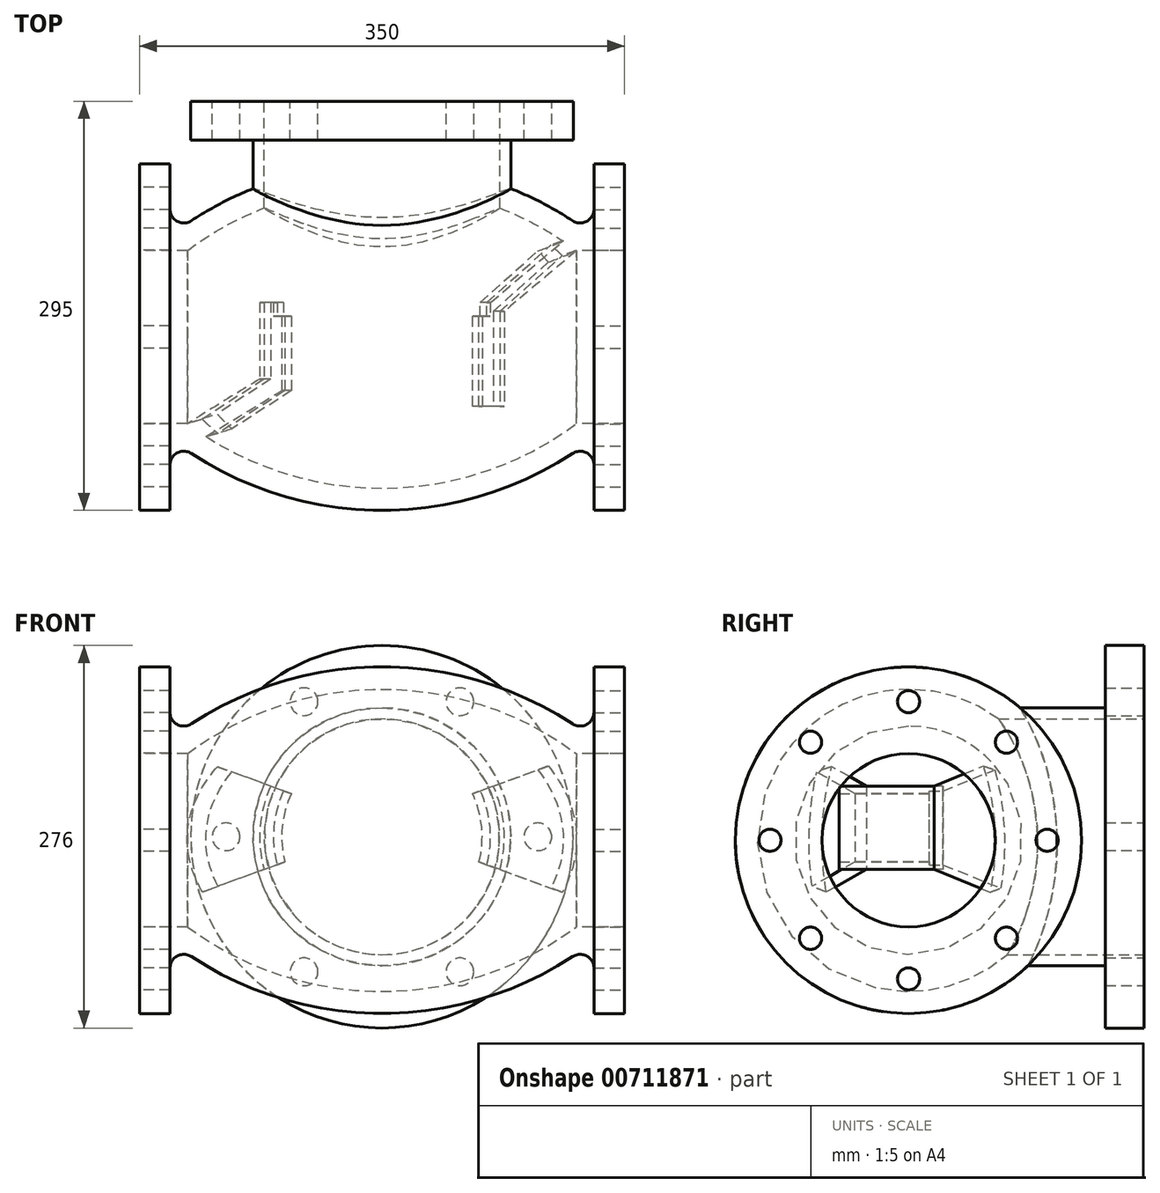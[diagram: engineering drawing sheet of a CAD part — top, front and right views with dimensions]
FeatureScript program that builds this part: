
annotation { "Feature Type Name" : "Feature", "Feature Type Description" : "" }
export const myFeature = defineFeature(function(context is Context, id is Id, definition is map)
    precondition{}
    {
        {
            var Q0;
            Q0=qCreatedBy(makeId("Front.planeOp"),FACE);
            var sketch = newSketch(context, id + "F0", { "sketchPlane" : qUnion([Q0])});
            skLineSegment(sketch, "E0", {"start": v(-230.6, 0) * mm, "end": v(175, 0) * mm, "construction": true});
            skLineSegment(sketch, "E1", {"start": v(0, 102.02) * mm, "end": v(0, 0) * mm, "construction": true});
            skLineSegment(sketch, "E2", {"start": v(0, 0) * mm, "end": v(0, -155.36) * mm, "construction": true});
            skPoint(sketch, "E3.orphan", {"position": v(-158.19, 0) * mm});
            skLineSegment(sketch, "E4", {"start": v(175, 0) * mm, "end": v(175, -62.5) * mm});
            skLineSegment(sketch, "E5", {"start": v(175, -62.5) * mm, "end": v(153, -62.5) * mm});
            skArc(sketch, "E6", {"start": v(-140.33, 0) * mm, "mid": v(0, -46.5) * mm, "end": v(140.33, 0) * mm});
            skLineSegment(sketch, "E7", {"start": v(-175, 0) * mm, "end": v(-175, -62.5) * mm});
            skLineSegment(sketch, "E8", {"start": v(-175, -62.5) * mm, "end": v(-153, -62.5) * mm});
            skLineSegment(sketch, "E9", {"start": v(-153, -62.5) * mm, "end": v(-153, -29.84) * mm});
            skLineSegment(sketch, "E10", {"start": v(153, -62.5) * mm, "end": v(153, -29.84) * mm});
            skArc(sketch, "E11", {"start": v(153, -29.84) * mm, "mid": v(147.75, -21.04) * mm, "end": v(137.52, -21.47) * mm});
            skArc(sketch, "E12.MirrorCS", {"start": v(-153, -29.84) * mm, "mid": v(-147.75, -21.04) * mm, "end": v(-137.52, -21.47) * mm});
            skArc(sketch, "E13.trimOffspring", {"start": v(-137.52, -21.47) * mm, "mid": v(0, -62.5) * mm, "end": v(137.52, -21.47) * mm});
            skLineSegment(sketch, "E14", {"start": v(175, 0) * mm, "end": v(140.33, 0) * mm});
            skLineSegment(sketch, "E15", {"start": v(-175, 0) * mm, "end": v(-140.33, 0) * mm});
            skLineSegment(sketch, "E16.0", {"start": v(-230.6, 62.5) * mm, "end": v(175, 62.5) * mm});
            skSolve(sketch);
        }
        {
            var Q0;
            Q0=makeQuery(id+"F0.imprint","IMPRINT",FACE,{"disambiguationData":[TD([[makeQuery(id+"F0.imprint","IMPRINT",EDGE,{"derivedFrom":sQuery(id+"F0.wireOp",EDGE,"E4")}),-1.0]])]});
            var Q1;
            Q1=sQuery(id+"F0.wireOp",EDGE,"E16.0");
            revolve(context, id + "F1", {"surfaceOperationType" : NewSurfaceOperationType.NEW, "entities" : qUnion([Q0]), "axis" : qUnion([Q1]), "revolveType" : RevolveType.FULL});
        }
        {
            var Q0;
            Q0=makeQuery(id+"F1.opRevolve","SWEPT_FACE",FACE,{"disambiguationData":[OSD([sQuery(id+"F0.wireOp",EDGE,"E4")])]});
            var sketch = newSketch(context, id + "F2", { "sketchPlane" : qUnion([Q0])});
            skCircle(sketch, "E17", {"center": v(0, 62.5) * mm, "radius": 100 * mm, "construction": true});
            skCircle(sketch, "E18", {"center": v(0, 162.5) * mm, "radius": 8 * mm});
            skSolve(sketch);
        }
        {
            var Q0;
            Q0 = qSketchRegion(id + "F2", true);
            extrude(context, id + "F3", {"entities" : qUnion([Q0]), "operationType" : NewBodyOperationType.REMOVE, "oppositeDirection" : true, "depth" : 25 * mm, "offsetDistance" : 25 * mm});
        }
        {
            var Q0;
            Q0=makeQuery(id+"F3.boolean.opBoolean","COPY",FACE,{"derivedFrom":makeQuery(id+"F3.opExtrude","SWEPT_FACE",FACE,{"disambiguationData":[OSD([sQuery(id+"F2.wireOp",EDGE,"E18")])]})});
            var Q1;
            Q1=makeQuery(id+"F1.opRevolve","SWEPT_EDGE",EDGE,{"disambiguationData":[OSD([sQuery(id+"F0.wireOp",EDGE,"E4"),sQuery(id+"F0.wireOp",EDGE,"E14")])]});
            circularPattern(context, id + "F4", {"patternType" : PatternType.FACE, "faces" : qUnion([Q0]), "axis" : qUnion([Q1]), "angle" : 360 * degree, "instanceCount" : 8, "equalSpace" : true});
        }
        {
            var Q0;
            Q0=makeQuery(id+"F1.opRevolve","SWEPT_FACE",FACE,{"disambiguationData":[OSD([sQuery(id+"F0.wireOp",EDGE,"E7")])]});
            var sketch = newSketch(context, id + "F5", { "sketchPlane" : qUnion([Q0])});
            skLineSegment(sketch, "E19", {"start": v(0, 62.5) * mm, "end": v(-100, 62.5) * mm, "construction": true});
            skCircle(sketch, "E20", {"center": v(-100, 62.5) * mm, "radius": 8 * mm});
            skSolve(sketch);
        }
        {
            var Q0;
            Q0 = qSketchRegion(id + "F5", true);
            extrude(context, id + "F6", {"entities" : qUnion([Q0]), "operationType" : NewBodyOperationType.REMOVE, "oppositeDirection" : true, "depth" : 25 * mm, "offsetDistance" : 25 * mm});
        }
        {
            var Q0;
            Q0=makeQuery(id+"F6.boolean.opBoolean","COPY",FACE,{"derivedFrom":makeQuery(id+"F6.opExtrude","SWEPT_FACE",FACE,{"disambiguationData":[OSD([sQuery(id+"F5.wireOp",EDGE,"E20")])]})});
            var Q1;
            Q1=makeQuery(id+"F1.opRevolve","SWEPT_EDGE",EDGE,{"disambiguationData":[OSD([sQuery(id+"F0.wireOp",EDGE,"E7"),sQuery(id+"F0.wireOp",EDGE,"E15")])]});
            circularPattern(context, id + "F7", {"patternType" : PatternType.FACE, "faces" : qUnion([Q0]), "axis" : qUnion([Q1]), "angle" : 360 * degree, "instanceCount" : 8, "equalSpace" : true});
        }
        {
            var Q0;
            Q0=qCreatedBy(makeId("Front.planeOp"),FACE);
            cPlane(context, id + "F8", {"entities" : qUnion([Q0]), "cplaneType" : CPlaneType.OFFSET, "offset" : 170 * mm, "oppositeDirection" : true, "width" : 150 * mm, "height" : 150 * mm});
        }
        {
            var Q0;
            Q0=qCreatedBy(id+"F8.planeOp",FACE);
            var sketch = newSketch(context, id + "F9", { "sketchPlane" : qUnion([Q0])});
            skLineSegment(sketch, "E21", {"start": v(0, 0) * mm, "end": v(0, 65) * mm, "construction": true});
            skLineSegment(sketch, "E22", {"start": v(0, 65) * mm, "end": v(175, 65) * mm, "construction": true});
            skCircle(sketch, "E23", {"center": v(0, 65) * mm, "radius": 85 * mm});
            skCircle(sketch, "E24", {"center": v(0, 65) * mm, "radius": 93 * mm});
            skSolve(sketch);
        }
        {
            var Q0;
            Q0 = qSketchRegion(id + "F9", true);
            var Q1;
            Q1=makeQuery(id+"F1.opRevolve","SWEPT_FACE",FACE,{"disambiguationData":[OSD([sQuery(id+"F0.wireOp",EDGE,"E13.trimOffspring")])]});
            extrude(context, id + "F10", {"entities" : qUnion([Q0]), "operationType" : NewBodyOperationType.ADD, "endBound" : BoundingType.UP_TO_SURFACE, "depth" : 25 * mm, "endBoundEntityFace" : qUnion([Q1]), "offsetDistance" : 25 * mm});
        }
        {
            var Q0;
            Q0=makeQuery(id+"F10.opExtrude","CAP_FACE",FACE,{"disambiguationData":[OSD([sQuery(id+"F9.wireOp",EDGE,"E23"),sQuery(id+"F9.wireOp",EDGE,"E24")])],"isStart":true});
            var sketch = newSketch(context, id + "F11", { "sketchPlane" : qUnion([Q0])});
            skCircle(sketch, "E25", {"center": v(0, 65) * mm, "radius": 85 * mm});
            skSolve(sketch);
        }
        {
            var Q0;
            Q0 = qSketchRegion(id + "F11", true);
            extrude(context, id + "F12", {"entities" : qUnion([Q0]), "operationType" : NewBodyOperationType.REMOVE, "oppositeDirection" : true, "depth" : 125 * mm, "offsetDistance" : 25 * mm});
        }
        {
            var Q0;
            Q0=makeQuery(id+"F10.opExtrude","CAP_FACE",FACE,{"disambiguationData":[OSD([sQuery(id+"F9.wireOp",EDGE,"E23"),sQuery(id+"F9.wireOp",EDGE,"E24")])],"isStart":true});
            var sketch = newSketch(context, id + "F13", { "sketchPlane" : qUnion([Q0])});
            skCircle(sketch, "E26", {"center": v(0, 65) * mm, "radius": 93 * mm});
            skCircle(sketch, "E27", {"center": v(0, 65) * mm, "radius": 138 * mm});
            skSolve(sketch);
        }
        {
            var Q0;
            Q0=makeQuery(id+"F13.imprint","IMPRINT",FACE,{"disambiguationData":[TD([[makeQuery(id+"F13.imprint","IMPRINT",EDGE,{"derivedFrom":sQuery(id+"F13.wireOp",EDGE,"E26")}),1.0]])]});
            extrude(context, id + "F14", {"entities" : qUnion([Q0]), "operationType" : NewBodyOperationType.ADD, "oppositeDirection" : true, "depth" : 28 * mm, "offsetDistance" : 25 * mm});
        }
        {
            var Q0;
            Q0=makeQuery(id+"F14.boolean.opBoolean","MERGE",FACE,{"derivedFrom":[makeQuery(id+"F10.opExtrude","CAP_FACE",FACE,{"disambiguationData":[OSD([sQuery(id+"F9.wireOp",EDGE,"E23"),sQuery(id+"F9.wireOp",EDGE,"E24")])],"isStart":true}),makeQuery(id+"F14.opExtrude","CAP_FACE",FACE,{"disambiguationData":[OSD([sQuery(id+"F13.wireOp",EDGE,"E26"),sQuery(id+"F13.wireOp",EDGE,"E27")])],"isStart":true})]});
            var sketch = newSketch(context, id + "F15", { "sketchPlane" : qUnion([Q0])});
            skLineSegment(sketch, "E28", {"start": v(0, 65) * mm, "end": v(-112.5, 65) * mm, "construction": true});
            skCircle(sketch, "E29", {"center": v(-112.5, 65) * mm, "radius": 10 * mm});
            skSolve(sketch);
        }
        {
            var Q0;
            Q0 = qSketchRegion(id + "F15", true);
            extrude(context, id + "F16", {"entities" : qUnion([Q0]), "operationType" : NewBodyOperationType.REMOVE, "endBound" : BoundingType.UP_TO_NEXT, "oppositeDirection" : true, "depth" : 25 * mm, "offsetDistance" : 25 * mm});
        }
        {
            var Q0;
            Q0=makeQuery(id+"F16.boolean.opBoolean","COPY",FACE,{"derivedFrom":makeQuery(id+"F16.opExtrude","SWEPT_FACE",FACE,{"disambiguationData":[OSD([sQuery(id+"F15.wireOp",EDGE,"E29")])]})});
            var Q1;
            Q1=makeQuery(id+"F10.opExtrude","CAP_EDGE",EDGE,{"disambiguationData":[OSD([sQuery(id+"F9.wireOp",EDGE,"E23")])],"isStart":true});
            circularPattern(context, id + "F17", {"patternType" : PatternType.FACE, "faces" : qUnion([Q0]), "axis" : qUnion([Q1]), "angle" : 360 * degree, "instanceCount" : 6, "equalSpace" : true});
        }
        {
            var Q0;
            Q0=makeQuery(id+"F14.boolean.opBoolean","MERGE",FACE,{"derivedFrom":[makeQuery(id+"F10.opExtrude","CAP_FACE",FACE,{"disambiguationData":[OSD([sQuery(id+"F9.wireOp",EDGE,"E23"),sQuery(id+"F9.wireOp",EDGE,"E24")])],"isStart":true}),makeQuery(id+"F14.opExtrude","CAP_FACE",FACE,{"disambiguationData":[OSD([sQuery(id+"F13.wireOp",EDGE,"E26"),sQuery(id+"F13.wireOp",EDGE,"E27")])],"isStart":true})]});
            var sketch = newSketch(context, id + "F18", { "sketchPlane" : qUnion([Q0])});
            skLineSegment(sketch, "E30", {"start": v(-112.5, 65) * mm, "end": v(112.5, 65) * mm, "construction": true});
            skCircle(sketch, "E31", {"center": v(0, 65) * mm, "radius": 112.5 * mm, "construction": true});
            skLineSegment(sketch, "E32", {"start": v(0, 251.95) * mm, "end": v(0, -108.2) * mm, "construction": true});
            skSolve(sketch);
        }
        {
            var Q0;
            Q0=sQuery(id+"F18.wireOp",EDGE,"E32");
            cPlane(context, id + "F19", {"entities" : qUnion([Q0]), "cplaneType" : CPlaneType.MID_PLANE, "offset" : 25 * mm, "width" : 150 * mm, "height" : 150 * mm});
        }
        {
            var Q0;
            Q0=qCreatedBy(id+"F19.planeOp",FACE);
            var sketch = newSketch(context, id + "F20", { "sketchPlane" : qUnion([Q0])});
            skLineSegment(sketch, "E33", {"start": v(88, -18.47) * mm, "end": v(88, 50) * mm});
            skLineSegment(sketch, "E34", {"start": v(88, 50) * mm, "end": v(72, 50) * mm});
            skLineSegment(sketch, "E35", {"start": v(72, 50) * mm, "end": v(72, -15) * mm});
            skLineSegment(sketch, "E36", {"start": v(72, -15) * mm, "end": v(78, -15) * mm});
            skLineSegment(sketch, "E37", {"start": v(78, -15) * mm, "end": v(78, -25) * mm});
            skLineSegment(sketch, "E38", {"start": v(88, -18.47) * mm, "end": v(140.2, -62.36) * mm});
            skLineSegment(sketch, "E39", {"start": v(78, -25) * mm, "end": v(132.09, -70.47) * mm});
            skLineSegment(sketch, "E40", {"start": v(140.2, -62.36) * mm, "end": v(140.55, -62.64) * mm});
            skLineSegment(sketch, "E41", {"start": v(140.55, -62.64) * mm, "end": v(132.09, -70.47) * mm});
            skLineSegment(sketch, "E42", {"start": v(-78, -25) * mm, "end": v(-78, -15) * mm});
            skLineSegment(sketch, "E43", {"start": v(-78, -15) * mm, "end": v(-72, -15) * mm});
            skLineSegment(sketch, "E44", {"start": v(-72, -15) * mm, "end": v(-72, 38.68) * mm});
            skLineSegment(sketch, "E45", {"start": v(-78, -25) * mm, "end": v(-88, -25) * mm});
            skLineSegment(sketch, "E46", {"start": v(-88, -25) * mm, "end": v(-88, 30.24) * mm});
            skLineSegment(sketch, "E47", {"start": v(-72, 38.68) * mm, "end": v(-127.74, 72.22) * mm});
            skLineSegment(sketch, "E48", {"start": v(-88, 30.24) * mm, "end": v(-141.08, 62.88) * mm});
            skLineSegment(sketch, "E49", {"start": v(-141.08, 62.88) * mm, "end": v(-127.74, 72.22) * mm});
            skSolve(sketch);
        }
        {
            var Q0;
            Q0=makeQuery(id+"F20.imprint","IMPRINT",FACE,{"disambiguationData":[TD([[makeQuery(id+"F20.imprint","IMPRINT",EDGE,{"derivedFrom":sQuery(id+"F20.wireOp",EDGE,"E33")}),1.0]])]});
            var Q1;
            Q1=makeQuery(id+"F20.imprint","IMPRINT",FACE,{"disambiguationData":[TD([[makeQuery(id+"F20.imprint","IMPRINT",EDGE,{"derivedFrom":sQuery(id+"F20.wireOp",EDGE,"E42")}),1.0]])]});
            var Q2;
            Q2=makeQuery(id+"F14.opExtrude","CAP_EDGE",EDGE,{"disambiguationData":[OSD([sQuery(id+"F13.wireOp",EDGE,"E27")])],"isStart":true});
            revolve(context, id + "F21", {"operationType" : NewBodyOperationType.ADD, "surfaceOperationType" : NewSurfaceOperationType.NEW, "entities" : qUnion([Q0, Q1]), "axis" : qUnion([Q2]), "revolveType" : RevolveType.SYMMETRIC, "angle" : 40 * degree});
        }
    });
